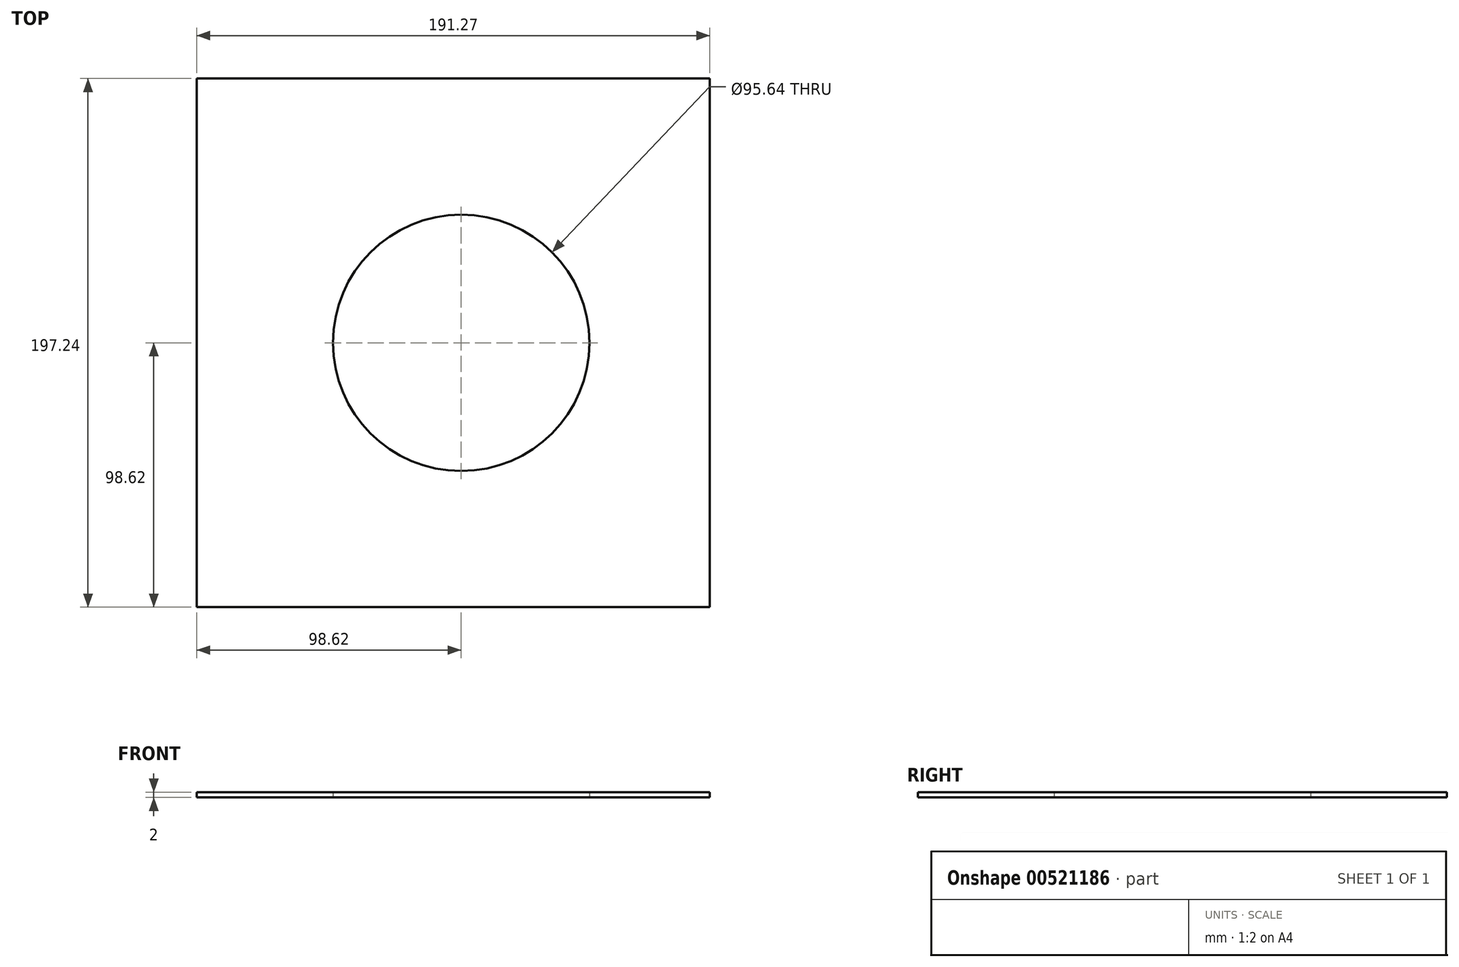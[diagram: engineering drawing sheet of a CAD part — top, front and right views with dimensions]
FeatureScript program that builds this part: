
annotation { "Feature Type Name" : "Feature", "Feature Type Description" : "" }
export const myFeature = defineFeature(function(context is Context, id is Id, definition is map)
    precondition{}
    {
        {
            assignVariable(context, id + "F0", {"name" : "Border", "anyValue" : 2});
        }
        {
            var Q0;
            Q0=qCreatedBy(makeId("Top.planeOp"),FACE);
            var sketch = newSketch(context, id + "F1", { "sketchPlane" : qUnion([Q0])});
            skLineSegment(sketch, "E0.bottom", {"start": v(-98.62, 98.62) * mm, "end": v(92.65, 98.62) * mm});
            skLineSegment(sketch, "E0.top", {"start": v(-98.62, -98.62) * mm, "end": v(92.65, -98.62) * mm});
            skLineSegment(sketch, "E0.left", {"start": v(-98.62, 98.62) * mm, "end": v(-98.62, -98.62) * mm});
            skLineSegment(sketch, "E0.right", {"start": v(92.65, 98.62) * mm, "end": v(92.65, -98.62) * mm});
            skCircle(sketch, "E1", {"center": v(0, 0) * mm, "radius": 47.82 * mm});
            skLineSegment(sketch, "E2", {"start": v(0, 98.62) * mm, "end": v(41.82, 23.19) * mm});
            skSolve(sketch);
        }
        {
            var Q0;
            Q0=makeQuery(id+"F1.imprint","IMPRINT",FACE,{"disambiguationData":[TD([[makeQuery(id+"F1.imprint","IMPRINT",EDGE,{"derivedFrom":sQuery(id+"F1.wireOp",EDGE,"E0.top")}),1.0]])]});
            extrude(context, id + "F2", {"entities" : qUnion([Q0]), "depth" : (getVariable(context, 'Border')) * mm, "offsetDistance" : 25.4 * mm});
        }
    });
